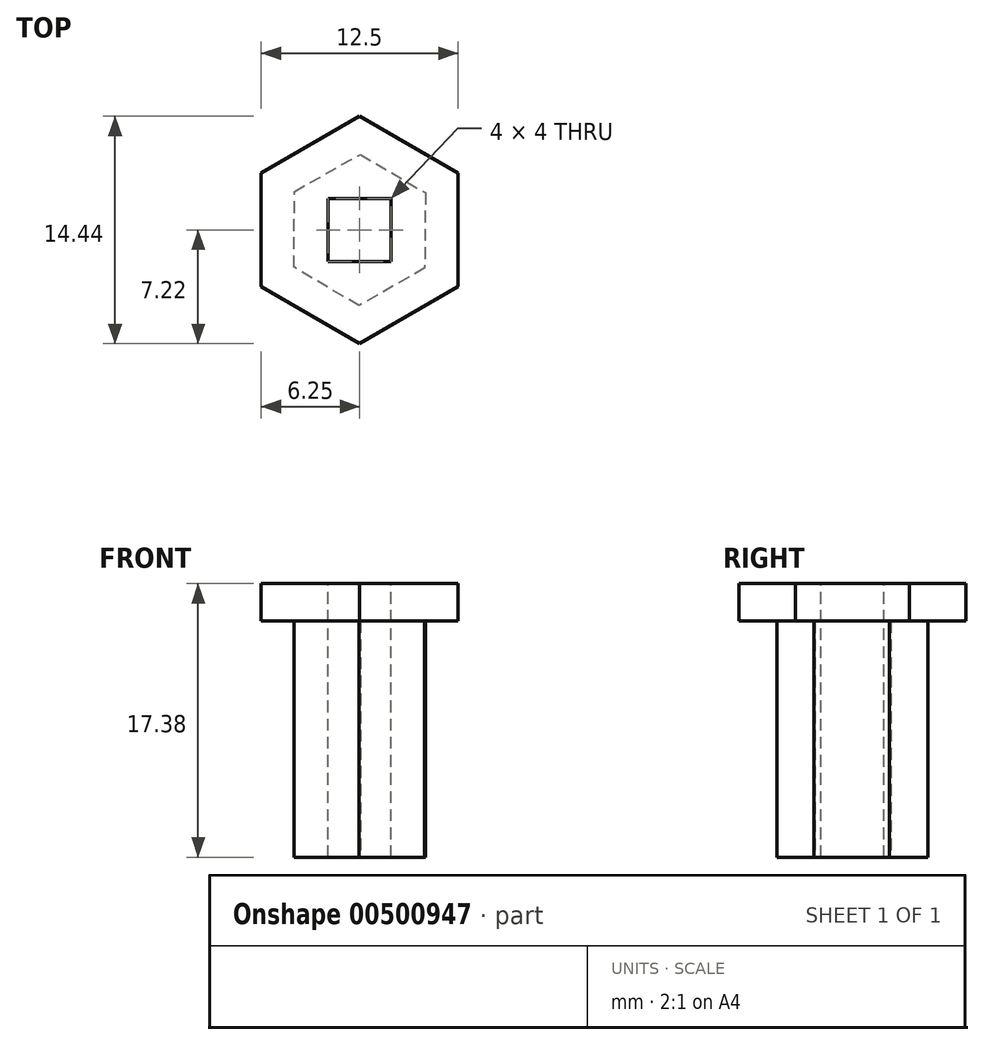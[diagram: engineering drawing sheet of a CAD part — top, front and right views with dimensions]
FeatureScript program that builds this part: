
annotation { "Feature Type Name" : "Feature", "Feature Type Description" : "" }
export const myFeature = defineFeature(function(context is Context, id is Id, definition is map)
    precondition{}
    {
        {
            var Q0;
            Q0=qCreatedBy(makeId("Top.planeOp"),FACE);
            var sketch = newSketch(context, id + "F0", { "sketchPlane" : qUnion([Q0])});
            skCircle(sketch, "E0.cCircle", {"center": v(0, 12.18) * mm, "radius": 4.16 * mm, "construction": true});
            skLineSegment(sketch, "E0.0", {"start": v(4.14, 9.74) * mm, "end": v(-0.04, 7.38) * mm});
            skLineSegment(sketch, "E0.1", {"start": v(-0.04, 7.38) * mm, "end": v(-4.18, 9.81) * mm});
            skLineSegment(sketch, "E0.2", {"start": v(-4.18, 9.81) * mm, "end": v(-4.14, 14.61) * mm});
            skLineSegment(sketch, "E0.3", {"start": v(-4.14, 14.61) * mm, "end": v(0.04, 16.98) * mm});
            skLineSegment(sketch, "E0.4", {"start": v(0.04, 16.98) * mm, "end": v(4.18, 14.54) * mm});
            skLineSegment(sketch, "E0.5", {"start": v(4.18, 14.54) * mm, "end": v(4.14, 9.74) * mm});
            skPoint(sketch, "E0.0.midPoint", {"position": v(2.05, 8.56) * mm});
            skSolve(sketch);
        }
        {
            var Q0;
            Q0=qSketchRegion(id+"F0",true);
            extrude(context, id + "F1", {"entities" : qUnion([Q0]), "depth" : 15 * mm});
        }
        {
            var Q0;
            Q0=makeQuery(id+"F1.opExtrude","CAP_FACE",FACE,{"disambiguationData":[OSD([sQuery(id+"F0.wireOp",EDGE,"E0.0"),sQuery(id+"F0.wireOp",EDGE,"E0.1"),sQuery(id+"F0.wireOp",EDGE,"E0.2"),sQuery(id+"F0.wireOp",EDGE,"E0.3"),sQuery(id+"F0.wireOp",EDGE,"E0.4"),sQuery(id+"F0.wireOp",EDGE,"E0.5")])],"isStart":false});
            var sketch = newSketch(context, id + "F2", { "sketchPlane" : qUnion([Q0])});
            skCircle(sketch, "E1.cCircle", {"center": v(0, 12.18) * mm, "radius": 6.25 * mm, "construction": true});
            skLineSegment(sketch, "E1.0", {"start": v(0, 19.4) * mm, "end": v(6.25, 15.79) * mm});
            skLineSegment(sketch, "E1.1", {"start": v(6.25, 15.79) * mm, "end": v(6.25, 8.57) * mm});
            skLineSegment(sketch, "E1.2", {"start": v(6.25, 8.57) * mm, "end": v(0, 4.96) * mm});
            skLineSegment(sketch, "E1.3", {"start": v(0, 4.96) * mm, "end": v(-6.25, 8.57) * mm});
            skLineSegment(sketch, "E1.4", {"start": v(-6.25, 8.57) * mm, "end": v(-6.25, 15.79) * mm});
            skLineSegment(sketch, "E1.5", {"start": v(-6.25, 15.79) * mm, "end": v(0, 19.4) * mm});
            skPoint(sketch, "E1.0.midPoint", {"position": v(3.12, 17.6) * mm});
            skSolve(sketch);
        }
        {
            var Q0;
            Q0=qSketchRegion(id+"F2",true);
            extrude(context, id + "F3", {"entities" : qUnion([Q0]), "operationType" : NewBodyOperationType.ADD, "depth" : 2.38 * mm});
        }
        {
            var Q0;
            Q0=makeQuery(id+"F3.opExtrude","CAP_FACE",FACE,{"disambiguationData":[OSD([sQuery(id+"F2.wireOp",EDGE,"E1.0"),sQuery(id+"F2.wireOp",EDGE,"E1.1"),sQuery(id+"F2.wireOp",EDGE,"E1.2"),sQuery(id+"F2.wireOp",EDGE,"E1.3"),sQuery(id+"F2.wireOp",EDGE,"E1.4"),sQuery(id+"F2.wireOp",EDGE,"E1.5")])],"isStart":false});
            var sketch = newSketch(context, id + "F4", { "sketchPlane" : qUnion([Q0])});
            skLineSegment(sketch, "E2.bottom", {"start": v(-2, 14.18) * mm, "end": v(2, 14.18) * mm});
            skLineSegment(sketch, "E2.top", {"start": v(-2, 10.18) * mm, "end": v(2, 10.18) * mm});
            skLineSegment(sketch, "E2.left", {"start": v(-2, 14.18) * mm, "end": v(-2, 10.18) * mm});
            skLineSegment(sketch, "E2.right", {"start": v(2, 14.18) * mm, "end": v(2, 10.18) * mm});
            skSolve(sketch);
        }
        {
            var Q0;
            Q0=qSketchRegion(id+"F4",true);
            extrude(context, id + "F5", {"entities" : qUnion([Q0]), "operationType" : NewBodyOperationType.REMOVE, "oppositeDirection" : true, "depth" : 18 * mm});
        }
    });
